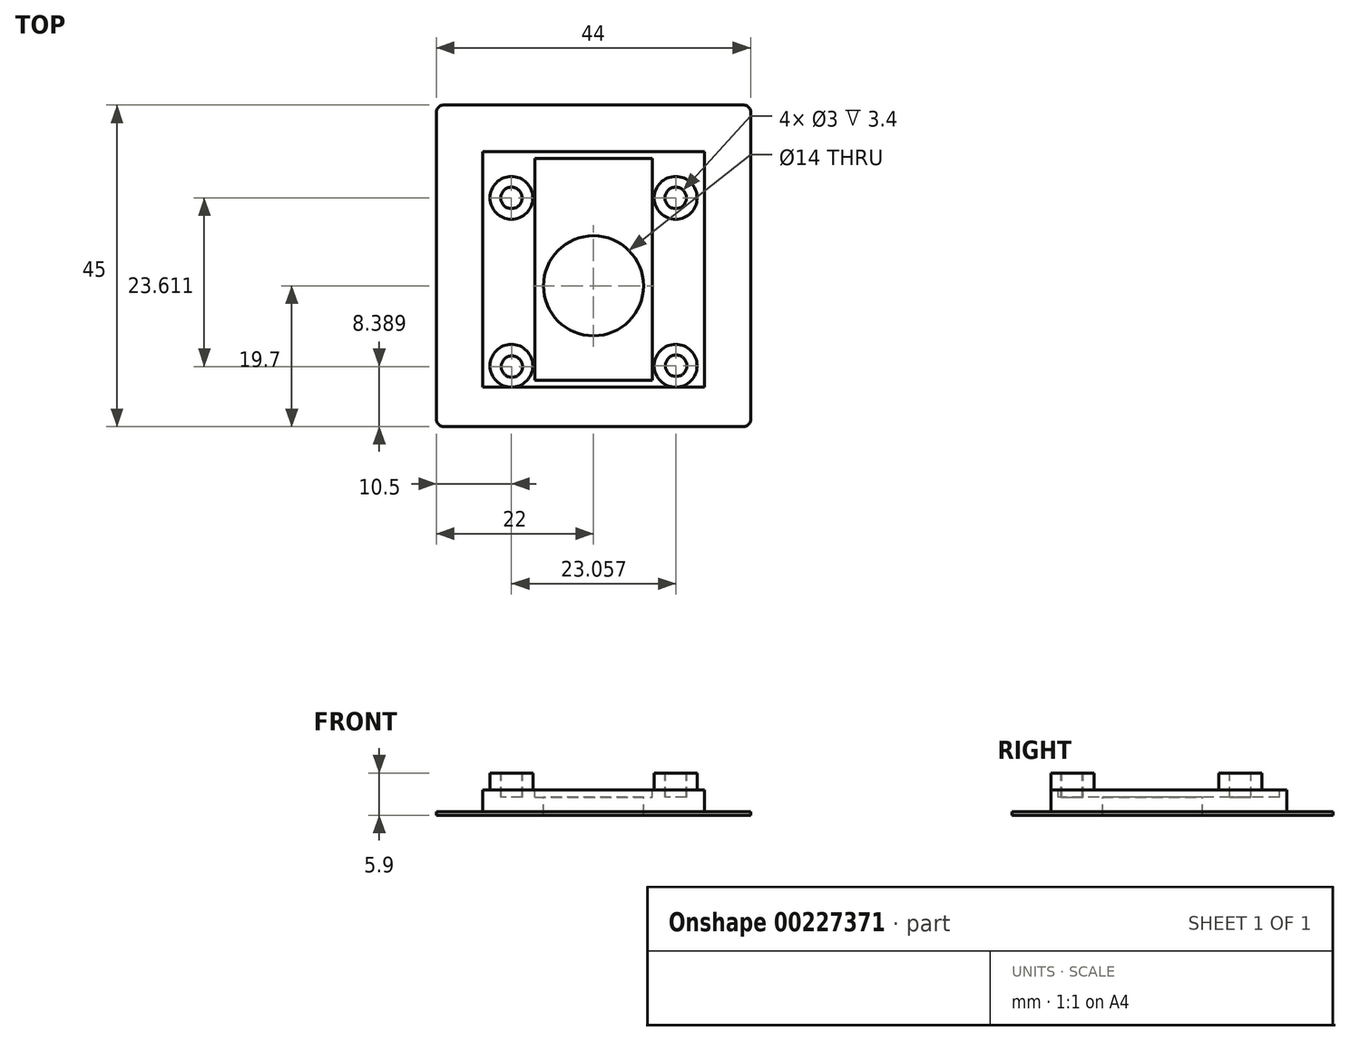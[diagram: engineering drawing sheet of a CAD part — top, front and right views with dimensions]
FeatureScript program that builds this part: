
annotation { "Feature Type Name" : "Feature", "Feature Type Description" : "" }
export const myFeature = defineFeature(function(context is Context, id is Id, definition is map)
    precondition{}
    {
        {
            var Q0;
            Q0=qCreatedBy(makeId("Top.planeOp"),FACE);
            var sketch = newSketch(context, id + "F0", { "sketchPlane" : qUnion([Q0])});
            skLineSegment(sketch, "E0.bottom", {"start": v(0, 0) * mm, "end": v(31, 0) * mm});
            skLineSegment(sketch, "E0.top", {"start": v(0, 33) * mm, "end": v(31, 33) * mm});
            skLineSegment(sketch, "E0.left", {"start": v(0, 0) * mm, "end": v(0, 33) * mm});
            skLineSegment(sketch, "E0.right", {"start": v(31, 0) * mm, "end": v(31, 33) * mm});
            skSolve(sketch);
        }
        {
            var Q0;
            Q0=qSketchRegion(id+"F0",true);
            extrude(context, id + "F1", {"entities" : qUnion([Q0]), "depth" : 2 * mm});
        }
        {
            var Q0;
            Q0=makeQuery(id+"F1.opExtrude","CAP_FACE",FACE,{"disambiguationData":[OSD([sQuery(id+"F0.wireOp",EDGE,"E0.bottom"),sQuery(id+"F0.wireOp",EDGE,"E0.top"),sQuery(id+"F0.wireOp",EDGE,"E0.left"),sQuery(id+"F0.wireOp",EDGE,"E0.right")])],"isStart":false});
            var sketch = newSketch(context, id + "F2", { "sketchPlane" : qUnion([Q0])});
            skCircle(sketch, "E1", {"center": v(4, 3) * mm, "radius": 3 * mm});
            skCircle(sketch, "E2", {"center": v(4, 26.5) * mm, "radius": 3 * mm});
            skCircle(sketch, "E3", {"center": v(27, 26.5) * mm, "radius": 3 * mm});
            skCircle(sketch, "E4", {"center": v(27, 3) * mm, "radius": 3 * mm});
            skSolve(sketch);
        }
        {
            var Q0;
            Q0=qSketchRegion(id+"F2",true);
            extrude(context, id + "F3", {"entities" : qUnion([Q0]), "operationType" : NewBodyOperationType.ADD, "depth" : 2.4 * mm});
        }
        {
            var Q0;
            Q0=makeQuery(id+"F1.opExtrude","CAP_FACE",FACE,{"disambiguationData":[OSD([sQuery(id+"F0.wireOp",EDGE,"E0.bottom"),sQuery(id+"F0.wireOp",EDGE,"E0.top"),sQuery(id+"F0.wireOp",EDGE,"E0.left"),sQuery(id+"F0.wireOp",EDGE,"E0.right")])],"isStart":false});
            var sketch = newSketch(context, id + "F4", { "sketchPlane" : qUnion([Q0])});
            skLineSegment(sketch, "E5.bottom", {"start": v(7.3, 32) * mm, "end": v(23.7, 32) * mm});
            skLineSegment(sketch, "E5.top", {"start": v(7.3, 1) * mm, "end": v(23.7, 1) * mm});
            skLineSegment(sketch, "E5.left", {"start": v(7.3, 32) * mm, "end": v(7.3, 1) * mm});
            skLineSegment(sketch, "E5.right", {"start": v(23.7, 32) * mm, "end": v(23.7, 1) * mm});
            skSolve(sketch);
        }
        {
            var Q0;
            Q0=makeQuery(id+"F4.imprint","IMPRINT",FACE,{"disambiguationData":[TD([[makeQuery(id+"F4.imprint","IMPRINT",EDGE,{"derivedFrom":sQuery(id+"F4.wireOp",EDGE,"E5.bottom")}),-1.0]])]});
            extrude(context, id + "F5", {"entities" : qUnion([Q0]), "operationType" : NewBodyOperationType.REMOVE, "oppositeDirection" : true, "depth" : 1 * mm});
        }
        {
            var Q0;
            Q0=makeQuery(id+"F3.opExtrude","CAP_FACE",FACE,{"disambiguationData":[OSD([sQuery(id+"F2.wireOp",EDGE,"E3")])],"isStart":false});
            var sketch = newSketch(context, id + "F6", { "sketchPlane" : qUnion([Q0])});
            skCircle(sketch, "E6", {"center": v(27, 26.5) * mm, "radius": 1.5 * mm});
            skSolve(sketch);
        }
        {
            var Q0;
            Q0=qSketchRegion(id+"F6",true);
            extrude(context, id + "F7", {"entities" : qUnion([Q0]), "operationType" : NewBodyOperationType.REMOVE, "oppositeDirection" : true, "depth" : 3.4 * mm});
        }
        {
            var Q0;
            Q0=makeQuery(id+"F3.opExtrude","CAP_FACE",FACE,{"disambiguationData":[OSD([sQuery(id+"F2.wireOp",EDGE,"E2")])],"isStart":false});
            var sketch = newSketch(context, id + "F8", { "sketchPlane" : qUnion([Q0])});
            skCircle(sketch, "E7", {"center": v(4, 26.5) * mm, "radius": 1.5 * mm});
            skCircle(sketch, "E8", {"center": v(4.06, 2.89) * mm, "radius": 1.5 * mm});
            skCircle(sketch, "E9", {"center": v(27.06, 3) * mm, "radius": 1.5 * mm});
            skSolve(sketch);
        }
        {
            var Q0;
            Q0=makeQuery(id+"F8.imprint","IMPRINT",FACE,{"disambiguationData":[TD([[makeQuery(id+"F8.imprint","IMPRINT",EDGE,{"derivedFrom":sQuery(id+"F8.wireOp",EDGE,"E7")}),1.0]])]});
            var Q1;
            Q1=makeQuery(id+"F8.imprint","IMPRINT",FACE,{"disambiguationData":[TD([[makeQuery(id+"F8.imprint","IMPRINT",EDGE,{"derivedFrom":sQuery(id+"F8.wireOp",EDGE,"E8")}),1.0]])]});
            var Q2;
            Q2=makeQuery(id+"F8.imprint","IMPRINT",FACE,{"disambiguationData":[TD([[makeQuery(id+"F8.imprint","IMPRINT",EDGE,{"derivedFrom":sQuery(id+"F8.wireOp",EDGE,"E9")}),1.0]])]});
            extrude(context, id + "F9", {"entities" : qUnion([Q0, Q1, Q2]), "operationType" : NewBodyOperationType.REMOVE, "oppositeDirection" : true, "depth" : 3.4 * mm});
        }
        {
            var Q0;
            Q0=makeQuery(id+"F5.boolean.opBoolean","COPY",FACE,{"derivedFrom":makeQuery(id+"F5.opExtrude","CAP_FACE",FACE,{"disambiguationData":[OSD([sQuery(id+"F4.wireOp",EDGE,"E5.bottom"),sQuery(id+"F4.wireOp",EDGE,"E5.top"),sQuery(id+"F4.wireOp",EDGE,"E5.left"),sQuery(id+"F4.wireOp",EDGE,"E5.right")])],"isStart":false})});
            var sketch = newSketch(context, id + "F10", { "sketchPlane" : qUnion([Q0])});
            skCircle(sketch, "E10", {"center": v(15.5, 14.2) * mm, "radius": 7 * mm});
            skSolve(sketch);
        }
        {
            var Q0;
            Q0=qSketchRegion(id+"F10",true);
            extrude(context, id + "F11", {"entities" : qUnion([Q0]), "operationType" : NewBodyOperationType.REMOVE, "oppositeDirection" : true, "depth" : 25 * mm});
        }
        {
            var Q0;
            Q0=makeQuery(id+"F1.opExtrude","CAP_FACE",FACE,{"disambiguationData":[OSD([sQuery(id+"F0.wireOp",EDGE,"E0.bottom"),sQuery(id+"F0.wireOp",EDGE,"E0.top"),sQuery(id+"F0.wireOp",EDGE,"E0.left"),sQuery(id+"F0.wireOp",EDGE,"E0.right")])],"isStart":true});
            extrude(context, id + "F12", {"entities" : qUnion([Q0]), "operationType" : NewBodyOperationType.ADD, "depth" : 1 * mm});
        }
        {
            var Q0;
            Q0=makeQuery(id+"F12.opExtrude","CAP_FACE",FACE,{"disambiguationData":[OSD([sQuery(id+"F0.wireOp",EDGE,"E0.bottom"),sQuery(id+"F0.wireOp",EDGE,"E0.top"),sQuery(id+"F0.wireOp",EDGE,"E0.left"),sQuery(id+"F0.wireOp",EDGE,"E0.right")])],"isStart":false});
            var sketch = newSketch(context, id + "F13", { "sketchPlane" : qUnion([Q0])});
            skLineSegment(sketch, "E11.bottom", {"start": v(-6.5, 5.5) * mm, "end": v(37.5, 5.5) * mm});
            skLineSegment(sketch, "E11.top", {"start": v(-6.5, -39.5) * mm, "end": v(37.5, -39.5) * mm});
            skLineSegment(sketch, "E11.left", {"start": v(-6.5, 5.5) * mm, "end": v(-6.5, -39.5) * mm});
            skLineSegment(sketch, "E11.right", {"start": v(37.5, 5.5) * mm, "end": v(37.5, -39.5) * mm});
            skSolve(sketch);
        }
        {
            var Q0;
            Q0=makeQuery(id+"F13.imprint","IMPRINT",FACE,{"disambiguationData":[TD([[makeQuery(id+"F13.imprint","IMPRINT",EDGE,{"derivedFrom":sQuery(id+"F13.wireOp",EDGE,"E11.bottom")}),-1.0]])]});
            var Q1;
            {var subQ3=sQuery(id+"F0.wireOp",EDGE,"E0.bottom");Q1=makeQuery(id+"F13.imprint","IMPRINT",FACE,{"disambiguationData":[TD([[makeQuery(id+"F13.imprint","IMPRINT",EDGE,{"derivedFrom":makeQuery(id+"F12.opExtrude","CAP_EDGE",EDGE,{"disambiguationData":[OSD([subQ3])],"isStart":false})}),-1.0]])]});}
            extrude(context, id + "F14", {"entities" : qUnion([Q0, Q1]), "operationType" : NewBodyOperationType.ADD, "depth" : 0.5 * mm});
        }
        {
            var Q0;
            Q0=makeQuery(id+"F14.opExtrude","SWEPT_EDGE",EDGE,{"disambiguationData":[OSD([sQuery(id+"F13.wireOp",EDGE,"E11.bottom"),sQuery(id+"F13.wireOp",EDGE,"E11.left")])]});
            var Q1;
            Q1=makeQuery(id+"F14.opExtrude","SWEPT_EDGE",EDGE,{"disambiguationData":[OSD([sQuery(id+"F13.wireOp",EDGE,"E11.bottom"),sQuery(id+"F13.wireOp",EDGE,"E11.right")])]});
            var Q2;
            Q2=makeQuery(id+"F14.opExtrude","SWEPT_EDGE",EDGE,{"disambiguationData":[OSD([sQuery(id+"F13.wireOp",EDGE,"E11.top"),sQuery(id+"F13.wireOp",EDGE,"E11.right")])]});
            var Q3;
            Q3=makeQuery(id+"F14.opExtrude","SWEPT_EDGE",EDGE,{"disambiguationData":[OSD([sQuery(id+"F13.wireOp",EDGE,"E11.top"),sQuery(id+"F13.wireOp",EDGE,"E11.left")])]});
            fillet(context, id + "F15", {"entities" : qUnion([Q0, Q1, Q2, Q3]), "radius" : 1 * mm, "tangentPropagation" : true, "allowEdgeOverflow" : false});
        }
    });
